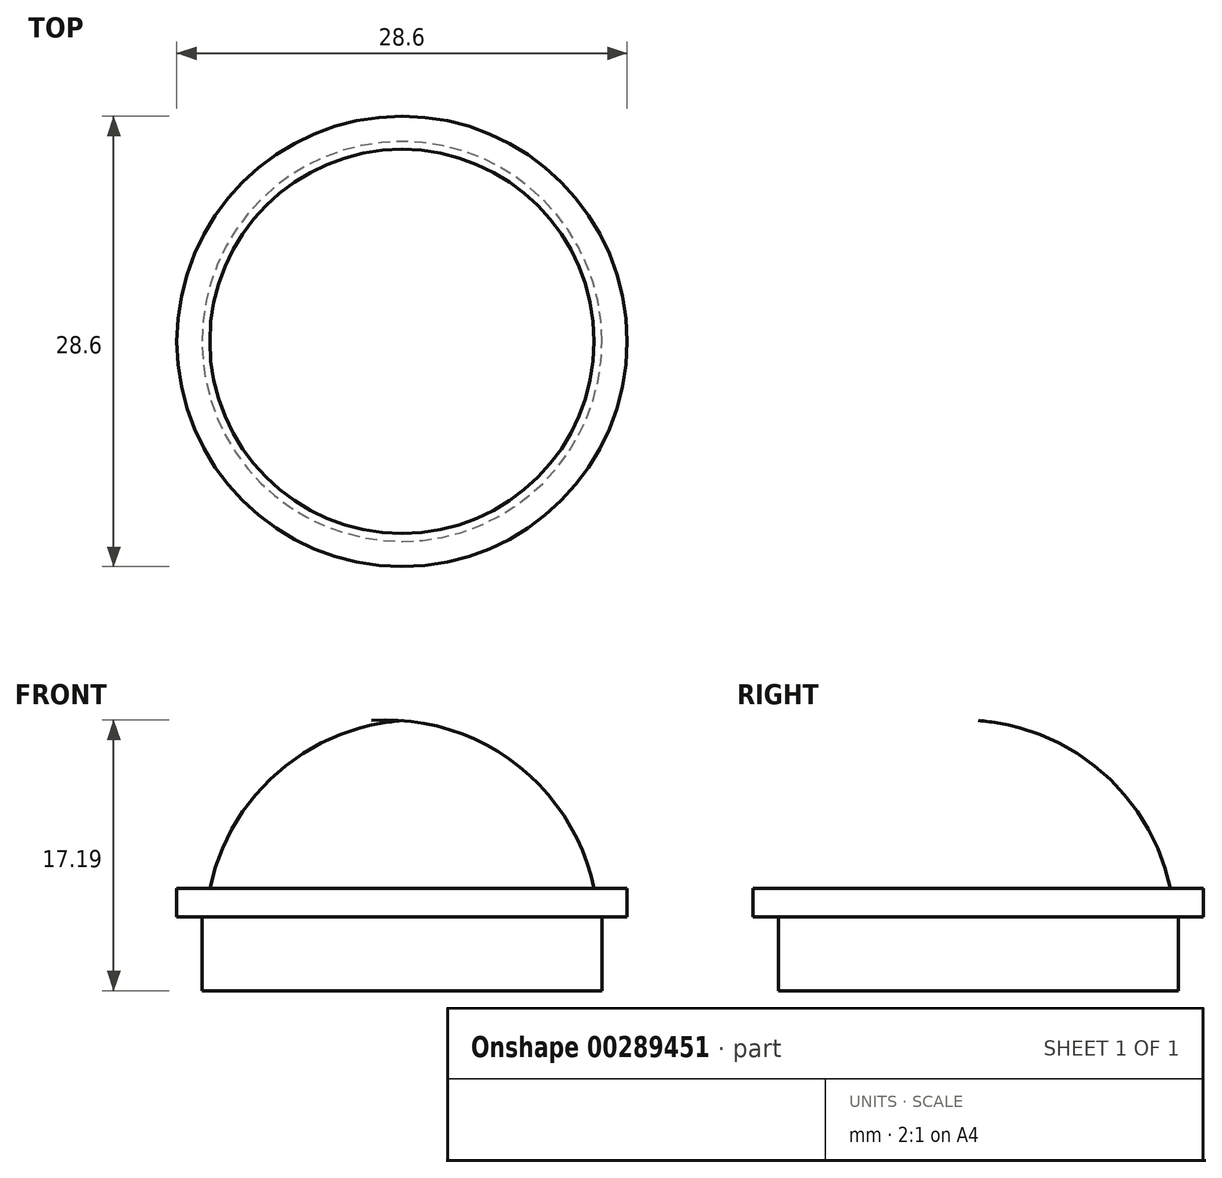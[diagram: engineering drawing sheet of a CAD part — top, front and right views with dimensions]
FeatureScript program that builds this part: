
annotation { "Feature Type Name" : "Feature", "Feature Type Description" : "" }
export const myFeature = defineFeature(function(context is Context, id is Id, definition is map)
    precondition{}
    {
        {
            var Q0;
            Q0=qCreatedBy(makeId("Front.planeOp"),FACE);
            var sketch = newSketch(context, id + "F0", { "sketchPlane" : qUnion([Q0])});
            skLineSegment(sketch, "E0", {"start": v(0, 0) * mm, "end": v(12.7, 0) * mm});
            skLineSegment(sketch, "E1", {"start": v(12.7, 0) * mm, "end": v(12.7, 4.7) * mm});
            skLineSegment(sketch, "E2", {"start": v(12.7, 4.7) * mm, "end": v(14.3, 4.7) * mm});
            skLineSegment(sketch, "E3", {"start": v(14.3, 4.7) * mm, "end": v(14.3, 6.5) * mm});
            skLineSegment(sketch, "E4", {"start": v(14.3, 6.5) * mm, "end": v(0, 6.5) * mm});
            skLineSegment(sketch, "E5", {"start": v(0, 6.5) * mm, "end": v(0, 0) * mm});
            skSolve(sketch);
        }
        {
            var Q0;
            Q0=makeQuery(id+"F0.imprint","IMPRINT",FACE,{"disambiguationData":[TD([[makeQuery(id+"F0.imprint","IMPRINT",EDGE,{"derivedFrom":sQuery(id+"F0.wireOp",EDGE,"E0")}),1.0]])]});
            var Q1;
            Q1=sQuery(id+"F0.wireOp",EDGE,"E5");
            revolve(context, id + "F1", {"entities" : qUnion([Q0]), "axis" : qUnion([Q1]), "revolveType" : RevolveType.FULL});
        }
        {
            var Q0;
            Q0=makeQuery(id+"F1.opRevolve","SWEPT_FACE",FACE,{"disambiguationData":[OSD([sQuery(id+"F0.wireOp",EDGE,"E4")])]});
            var sketch = newSketch(context, id + "F2", { "sketchPlane" : qUnion([Q0])});
            skCircle(sketch, "E6", {"center": v(0, 0) * mm, "radius": 12.49 * mm});
            skSolve(sketch);
        }
        {
            var Q0;
            Q0=qCreatedBy(makeId("Right.planeOp"),FACE);
            var sketch = newSketch(context, id + "F3", { "sketchPlane" : qUnion([Q0])});
            skArc(sketch, "E7", {"start": v(12.32, 5.86) * mm, "mid": v(8.13, 13.65) * mm, "end": v(0, 17.15) * mm});
            skLineSegment(sketch, "E8", {"start": v(12.32, 5.86) * mm, "end": v(0, 5.86) * mm});
            skLineSegment(sketch, "E9", {"start": v(0, 5.86) * mm, "end": v(0, 17.15) * mm});
            skSolve(sketch);
        }
        {
            var Q0;
            Q0=makeQuery(id+"F3.imprint","IMPRINT",FACE,{"disambiguationData":[TD([[makeQuery(id+"F3.imprint","IMPRINT",EDGE,{"derivedFrom":sQuery(id+"F3.wireOp",EDGE,"E7")}),1.0]])]});
            var Q1;
            Q1=sQuery(id+"F3.wireOp",EDGE,"E9");
            revolve(context, id + "F4", {"operationType" : NewBodyOperationType.ADD, "entities" : qUnion([Q0]), "axis" : qUnion([Q1]), "revolveType" : RevolveType.FULL});
        }
    });
